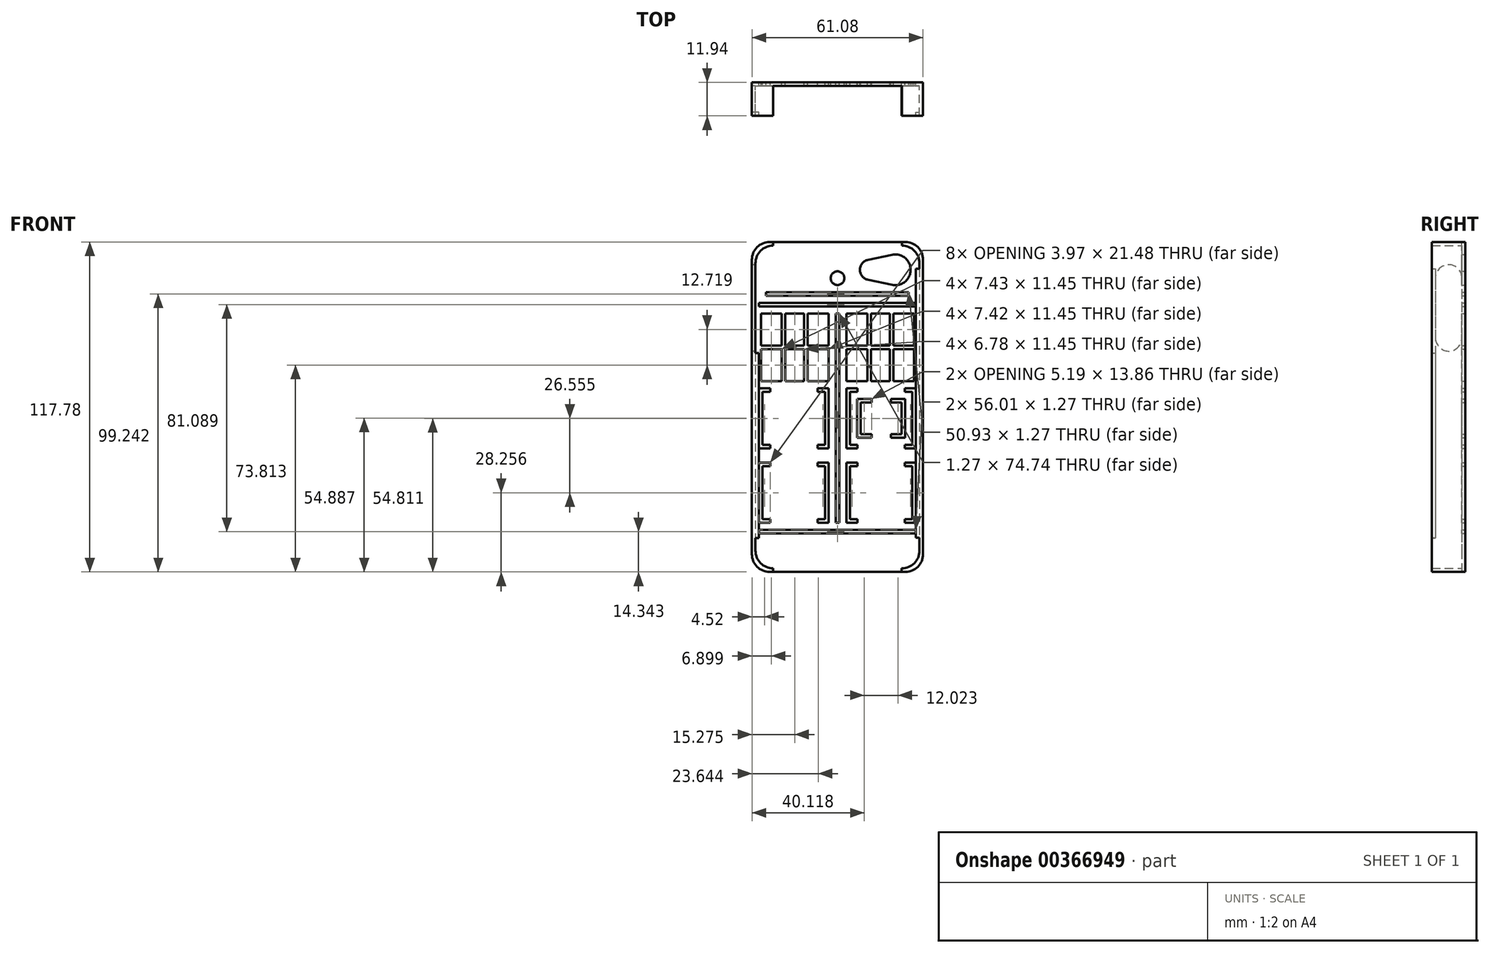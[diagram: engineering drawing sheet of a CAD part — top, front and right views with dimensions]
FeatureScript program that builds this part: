
annotation { "Feature Type Name" : "Feature", "Feature Type Description" : "" }
export const myFeature = defineFeature(function(context is Context, id is Id, definition is map)
    precondition{}
    {
        {
            var Q0;
            Q0=qCreatedBy(makeId("Front.planeOp"),FACE);
            var sketch = newSketch(context, id + "F0", { "sketchPlane" : qUnion([Q0])});
            skLineSegment(sketch, "E0.left", {"start": v(-75.12, 56.4) * mm, "end": v(-75.12, -46.14) * mm});
            skLineSegment(sketch, "E0.right", {"start": v(-16.58, 56.4) * mm, "end": v(-16.58, -46.14) * mm});
            skPoint(sketch, "E1.visualSharp", {"position": v(-16.58, 62.75) * mm});
            skArc(sketch, "E1.filletArc", {"start": v(-16.58, 56.4) * mm, "mid": v(-18.43, 60.88) * mm, "end": v(-22.9, 62.75) * mm});
            skPoint(sketch, "E2.visualSharp", {"position": v(-75.12, 62.75) * mm});
            skArc(sketch, "E2.filletArc", {"start": v(-68.77, 62.75) * mm, "mid": v(-73.26, 60.89) * mm, "end": v(-75.12, 56.4) * mm});
            skPoint(sketch, "E3.visualSharp", {"position": v(-75.12, -52.5) * mm});
            skArc(sketch, "E3.filletArc", {"start": v(-75.12, -46.14) * mm, "mid": v(-73.26, -50.63) * mm, "end": v(-68.77, -52.5) * mm});
            skPoint(sketch, "E4.visualSharp", {"position": v(-16.58, -52.5) * mm});
            skArc(sketch, "E4.filletArc", {"start": v(-22.93, -52.5) * mm, "mid": v(-18.44, -50.63) * mm, "end": v(-16.58, -46.14) * mm});
            skLineSegment(sketch, "E5.bottom", {"start": v(-70.04, 64.02) * mm, "end": v(-68.77, 64.02) * mm});
            skLineSegment(sketch, "E5.top", {"start": v(-70.04, -53.76) * mm, "end": v(-68.77, -53.76) * mm});
            skLineSegment(sketch, "E5.left", {"start": v(-76.4, 57.67) * mm, "end": v(-76.4, -47.41) * mm});
            skLineSegment(sketch, "E5.right", {"start": v(-15.3, 57.67) * mm, "end": v(-15.3, -47.41) * mm});
            skPoint(sketch, "E6.visualSharp", {"position": v(-15.3, 64.02) * mm});
            skArc(sketch, "E6.filletArc", {"start": v(-15.3, 57.67) * mm, "mid": v(-17.17, 62.16) * mm, "end": v(-21.66, 64.02) * mm});
            skPoint(sketch, "E7.visualSharp", {"position": v(-76.4, 64.02) * mm});
            skArc(sketch, "E7.filletArc", {"start": v(-70.04, 64.02) * mm, "mid": v(-74.53, 62.16) * mm, "end": v(-76.4, 57.67) * mm});
            skPoint(sketch, "E8.visualSharp", {"position": v(-76.4, -53.76) * mm});
            skArc(sketch, "E8.filletArc", {"start": v(-76.4, -47.41) * mm, "mid": v(-74.53, -51.9) * mm, "end": v(-70.04, -53.76) * mm});
            skPoint(sketch, "E9.visualSharp", {"position": v(-15.3, -53.76) * mm});
            skArc(sketch, "E9.filletArc", {"start": v(-21.66, -53.76) * mm, "mid": v(-17.17, -51.9) * mm, "end": v(-15.3, -47.41) * mm});
            skLineSegment(sketch, "E10", {"start": v(-68.77, -52.5) * mm, "end": v(-68.77, -53.76) * mm});
            skLineSegment(sketch, "E11", {"start": v(-22.93, -52.5) * mm, "end": v(-22.93, -53.76) * mm});
            skLineSegment(sketch, "E12.trimOffspring", {"start": v(-22.93, -53.76) * mm, "end": v(-21.66, -53.76) * mm});
            skLineSegment(sketch, "E13", {"start": v(-68.77, 62.75) * mm, "end": v(-68.77, 64.02) * mm});
            skLineSegment(sketch, "E14", {"start": v(-22.9, 62.75) * mm, "end": v(-22.9, 64.02) * mm});
            skLineSegment(sketch, "E15.trimOffspring", {"start": v(-22.9, 64.02) * mm, "end": v(-21.66, 64.02) * mm});
            skLineSegment(sketch, "E16", {"start": v(-68.77, 64.02) * mm, "end": v(-22.9, 64.02) * mm});
            skLineSegment(sketch, "E17", {"start": v(-68.77, -53.76) * mm, "end": v(-22.93, -53.76) * mm});
            skCircle(sketch, "E18", {"center": v(-25.24, 54.09) * mm, "radius": 5.48 * mm});
            skCircle(sketch, "E19", {"center": v(-34.23, 54.09) * mm, "radius": 3.64 * mm});
            skLineSegment(sketch, "E20", {"start": v(-26.36, 59.46) * mm, "end": v(-34.97, 57.65) * mm});
            skLineSegment(sketch, "E21", {"start": v(-26.36, 48.72) * mm, "end": v(-34.97, 50.53) * mm});
            skLineSegment(sketch, "E22", {"start": v(-22.9, 62.75) * mm, "end": v(-68.77, 62.75) * mm});
            skSolve(sketch);
        }
        {
            var Q0;
            Q0=makeQuery(id+"F0.imprint","IMPRINT",FACE,{"disambiguationData":[TD([[makeQuery(id+"F0.imprint","IMPRINT",EDGE,{"derivedFrom":sQuery(id+"F0.wireOp",EDGE,"E0.left")}),1.0]])]});
            extrude(context, id + "F1", {"entities" : qUnion([Q0]), "depth" : 1.27 * mm});
        }
        {
            var Q0;
            Q0=makeQuery(id+"F0.imprint","IMPRINT",FACE,{"disambiguationData":[TD([[makeQuery(id+"F0.imprint","IMPRINT",EDGE,{"derivedFrom":sQuery(id+"F0.wireOp",EDGE,"E0.left")}),-1.0]])]});
            var Q1;
            Q1=makeQuery(id+"F0.imprint","IMPRINT",FACE,{"disambiguationData":[TD([[makeQuery(id+"F0.imprint","IMPRINT",EDGE,{"derivedFrom":sQuery(id+"F0.wireOp",EDGE,"E0.right")}),1.0]])]});
            extrude(context, id + "F2", {"entities" : qUnion([Q0, Q1]), "operationType" : NewBodyOperationType.ADD, "depth" : 11.94 * mm});
        }
        {
            var Q0;
            Q0=makeQuery(id+"F2.opExtrude","SWEPT_FACE",FACE,{"disambiguationData":[OSD([sQuery(id+"F0.wireOp",EDGE,"E5.left")])]});
            var sketch = newSketch(context, id + "F3", { "sketchPlane" : qUnion([Q0])});
            skCircle(sketch, "E23", {"center": v(5.97, 51.22) * mm, "radius": 4.7 * mm});
            skCircle(sketch, "E24", {"center": v(5.97, 29.75) * mm, "radius": 4.7 * mm});
            skLineSegment(sketch, "E25", {"start": v(1.27, 51.22) * mm, "end": v(1.27, 29.75) * mm});
            skLineSegment(sketch, "E26", {"start": v(10.67, 29.75) * mm, "end": v(10.67, 51.22) * mm});
            skSolve(sketch);
        }
        {
            var Q0;
            {var subQ0=sQuery(id+"F3.wireOp",EDGE,"E25");Q0=makeQuery(id+"F3.imprint","IMPRINT",FACE,{"disambiguationData":[TD([[makeQuery(id+"F3.imprint","IMPRINT",EDGE,{"derivedFrom":subQ0}),1.0]])]});}
            var Q1;
            {var subQ0=sQuery(id+"F3.wireOp",EDGE,"E23");var subQ1=makeQuery(id+"F3.imprint","INTERSECT",VERTEX,{"derivedFrom":[subQ0,sQuery(id+"F3.wireOp",EDGE,"E25")]});Q1=makeQuery(id+"F3.imprint","IMPRINT",FACE,{"disambiguationData":[TD([[makeQuery(id+"F3.imprint","IMPRINT",EDGE,{"disambiguationData":[TD([[subQ1,1.0]])],"derivedFrom":subQ0}),1.0]])]});}
            var Q2;
            {var subQ0=sQuery(id+"F3.wireOp",EDGE,"E24");var subQ1=makeQuery(id+"F3.imprint","INTERSECT",VERTEX,{"derivedFrom":[subQ0,sQuery(id+"F3.wireOp",EDGE,"E25")]});Q2=makeQuery(id+"F3.imprint","IMPRINT",FACE,{"disambiguationData":[TD([[makeQuery(id+"F3.imprint","IMPRINT",EDGE,{"disambiguationData":[TD([[subQ1,1.0]])],"derivedFrom":subQ0}),1.0]])]});}
            extrude(context, id + "F4", {"entities" : qUnion([Q0, Q1, Q2]), "operationType" : NewBodyOperationType.REMOVE, "oppositeDirection" : true, "depth" : 25.4 * mm});
        }
        {
            var Q0;
            Q0=makeQuery(id+"F0.imprint","IMPRINT",FACE,{"disambiguationData":[TD([[makeQuery(id+"F0.imprint","IMPRINT",EDGE,{"derivedFrom":sQuery(id+"F0.wireOp",EDGE,"E0.right")}),-1.0]])]});
            var Q1;
            Q1=makeQuery(id+"F0.imprint","IMPRINT",FACE,{"disambiguationData":[TD([[makeQuery(id+"F0.imprint","IMPRINT",EDGE,{"derivedFrom":sQuery(id+"F0.wireOp",EDGE,"E13")}),-1.0]])]});
            extrude(context, id + "F5", {"entities" : qUnion([Q0, Q1]), "depth" : 1.27 * mm});
        }
        {
            var Q0;
            Q0=makeQuery(id+"F2.opExtrude","SWEPT_FACE",FACE,{"disambiguationData":[OSD([sQuery(id+"F0.wireOp",EDGE,"E0.left")])]});
            var sketch = newSketch(context, id + "F6", { "sketchPlane" : qUnion([Q0])});
            skLineSegment(sketch, "E27.bottom", {"start": v(-11.94, 24.38) * mm, "end": v(-10.67, 24.38) * mm});
            skLineSegment(sketch, "E27.top", {"start": v(-11.94, -41.62) * mm, "end": v(-10.67, -41.62) * mm});
            skLineSegment(sketch, "E27.left", {"start": v(-11.94, 24.38) * mm, "end": v(-11.94, -41.62) * mm});
            skLineSegment(sketch, "E27.right", {"start": v(-10.67, 24.38) * mm, "end": v(-10.67, -41.62) * mm});
            skSolve(sketch);
        }
        {
            var Q0;
            Q0=makeQuery(id+"F6.imprint","IMPRINT",FACE,{"disambiguationData":[TD([[makeQuery(id+"F6.imprint","IMPRINT",EDGE,{"derivedFrom":sQuery(id+"F6.wireOp",EDGE,"E27.bottom")}),-1.0]])]});
            extrude(context, id + "F7", {"entities" : qUnion([Q0]), "operationType" : NewBodyOperationType.ADD, "depth" : 1.27 * mm});
        }
        {
            var Q0;
            Q0=makeQuery(id+"F2.opExtrude","SWEPT_FACE",FACE,{"disambiguationData":[OSD([sQuery(id+"F0.wireOp",EDGE,"E0.right")])]});
            var sketch = newSketch(context, id + "F8", { "sketchPlane" : qUnion([Q0])});
            skLineSegment(sketch, "E28.bottom", {"start": v(11.94, 54.52) * mm, "end": v(10.67, 54.52) * mm});
            skLineSegment(sketch, "E28.top", {"start": v(11.94, -41.5) * mm, "end": v(10.67, -41.5) * mm});
            skLineSegment(sketch, "E28.left", {"start": v(11.94, 54.52) * mm, "end": v(11.94, -41.5) * mm});
            skLineSegment(sketch, "E28.right", {"start": v(10.67, 54.52) * mm, "end": v(10.67, -41.5) * mm});
            skSolve(sketch);
        }
        {
            var Q0;
            Q0=makeQuery(id+"F8.imprint","IMPRINT",FACE,{"disambiguationData":[TD([[makeQuery(id+"F8.imprint","IMPRINT",EDGE,{"derivedFrom":sQuery(id+"F8.wireOp",EDGE,"E28.bottom")}),1.0]])]});
            extrude(context, id + "F9", {"entities" : qUnion([Q0]), "operationType" : NewBodyOperationType.ADD, "depth" : 1.27 * mm});
        }
        {
            var Q0;
            {var subQ0=sQuery(id+"F0.wireOp",EDGE,"E14");var subQ1=sQuery(id+"F0.wireOp",EDGE,"E11");var subQ2=sQuery(id+"F0.wireOp",EDGE,"E4.filletArc");var subQ3=sQuery(id+"F0.wireOp",EDGE,"E1.filletArc");var subQ4=sQuery(id+"F0.wireOp",EDGE,"E0.right");var subQ5=sQuery(id+"F0.wireOp",EDGE,"E13");var subQ6=sQuery(id+"F0.wireOp",EDGE,"E10");var subQ7=sQuery(id+"F0.wireOp",EDGE,"E3.filletArc");var subQ8=sQuery(id+"F0.wireOp",EDGE,"E2.filletArc");var subQ9=sQuery(id+"F0.wireOp",EDGE,"E0.left");Q0=makeQuery(id+"F2.boolean.opBoolean","MERGE",FACE,{"derivedFrom":[makeQuery(id+"F1.opExtrude","CAP_FACE",FACE,{"disambiguationData":[OSD([subQ9,subQ4,subQ3,subQ8,subQ7,subQ2,subQ6,subQ1,subQ5,subQ0,sQuery(id+"F0.wireOp",EDGE,"E16"),sQuery(id+"F0.wireOp",EDGE,"E17"),sQuery(id+"F0.wireOp",EDGE,"E18"),sQuery(id+"F0.wireOp",EDGE,"E19"),sQuery(id+"F0.wireOp",EDGE,"E20"),sQuery(id+"F0.wireOp",EDGE,"E21")])],"isStart":true}),makeQuery(id+"F2.opExtrude","CAP_FACE",FACE,{"disambiguationData":[OSD([subQ9,subQ8,subQ7,sQuery(id+"F0.wireOp",EDGE,"E5.bottom"),sQuery(id+"F0.wireOp",EDGE,"E5.top"),sQuery(id+"F0.wireOp",EDGE,"E5.left"),sQuery(id+"F0.wireOp",EDGE,"E7.filletArc"),sQuery(id+"F0.wireOp",EDGE,"E8.filletArc"),subQ6,subQ5])],"isStart":true}),makeQuery(id+"F2.opExtrude","CAP_FACE",FACE,{"disambiguationData":[OSD([subQ4,subQ3,subQ2,sQuery(id+"F0.wireOp",EDGE,"E5.right"),sQuery(id+"F0.wireOp",EDGE,"E6.filletArc"),sQuery(id+"F0.wireOp",EDGE,"E9.filletArc"),subQ1,sQuery(id+"F0.wireOp",EDGE,"E12.trimOffspring"),subQ0,sQuery(id+"F0.wireOp",EDGE,"E15.trimOffspring")])],"isStart":true})]});}
            var sketch = newSketch(context, id + "F10", { "sketchPlane" : qUnion([Q0])});
            skLineSegment(sketch, "E29", {"start": v(45.85, 64.02) * mm, "end": v(45.85, -53.76) * mm});
            skLineSegment(sketch, "E30.bottom", {"start": v(18.5, 38.5) * mm, "end": v(42.66, 38.5) * mm});
            skLineSegment(sketch, "E30.top", {"start": v(18.5, 14.33) * mm, "end": v(42.66, 14.33) * mm});
            skLineSegment(sketch, "E30.left", {"start": v(18.5, 38.5) * mm, "end": v(18.5, 14.33) * mm});
            skLineSegment(sketch, "E30.right", {"start": v(42.66, 38.5) * mm, "end": v(42.66, 14.33) * mm});
            skLineSegment(sketch, "E31.bottom", {"start": v(49.04, 38.5) * mm, "end": v(73.2, 38.5) * mm});
            skLineSegment(sketch, "E31.top", {"start": v(49.04, 14.33) * mm, "end": v(73.2, 14.33) * mm});
            skLineSegment(sketch, "E31.left", {"start": v(49.04, 38.5) * mm, "end": v(49.04, 14.33) * mm});
            skLineSegment(sketch, "E31.right", {"start": v(73.2, 38.5) * mm, "end": v(73.2, 14.33) * mm});
            skLineSegment(sketch, "E32", {"start": v(18.5, 38.5) * mm, "end": v(15.3, 38.5) * mm});
            skLineSegment(sketch, "E33", {"start": v(42.66, 38.5) * mm, "end": v(45.85, 38.5) * mm});
            skLineSegment(sketch, "E34", {"start": v(45.85, 38.5) * mm, "end": v(49.04, 38.5) * mm});
            skLineSegment(sketch, "E35", {"start": v(73.2, 38.5) * mm, "end": v(76.4, 38.5) * mm});
            skLineSegment(sketch, "E36", {"start": v(18.5, 26.41) * mm, "end": v(42.66, 26.41) * mm});
            skLineSegment(sketch, "E37", {"start": v(26.55, 38.5) * mm, "end": v(26.55, 14.33) * mm});
            skLineSegment(sketch, "E38", {"start": v(34.6, 38.5) * mm, "end": v(34.6, 14.33) * mm});
            skLineSegment(sketch, "E39", {"start": v(25.91, 38.5) * mm, "end": v(25.91, 26.41) * mm});
            skLineSegment(sketch, "E40", {"start": v(27.18, 38.5) * mm, "end": v(27.18, 26.41) * mm});
            skLineSegment(sketch, "E41", {"start": v(33.96, 38.5) * mm, "end": v(33.96, 26.41) * mm});
            skLineSegment(sketch, "E42", {"start": v(35.23, 38.5) * mm, "end": v(35.23, 26.41) * mm});
            skLineSegment(sketch, "E43", {"start": v(18.5, 27.05) * mm, "end": v(42.66, 27.05) * mm});
            skLineSegment(sketch, "E44", {"start": v(25.91, 26.41) * mm, "end": v(25.91, 14.33) * mm});
            skLineSegment(sketch, "E45", {"start": v(27.18, 26.41) * mm, "end": v(27.18, 14.33) * mm});
            skLineSegment(sketch, "E46", {"start": v(33.96, 26.41) * mm, "end": v(33.96, 14.33) * mm});
            skLineSegment(sketch, "E47", {"start": v(35.23, 26.41) * mm, "end": v(35.23, 14.33) * mm});
            skLineSegment(sketch, "E48", {"start": v(18.5, 25.78) * mm, "end": v(42.66, 25.78) * mm});
            skLineSegment(sketch, "E49", {"start": v(49.04, 26.41) * mm, "end": v(73.2, 26.41) * mm});
            skLineSegment(sketch, "E50", {"start": v(57.09, 38.5) * mm, "end": v(57.09, 14.33) * mm});
            skLineSegment(sketch, "E51", {"start": v(65.14, 38.5) * mm, "end": v(65.14, 14.33) * mm});
            skLineSegment(sketch, "E52", {"start": v(56.45, 38.5) * mm, "end": v(56.45, 14.33) * mm});
            skLineSegment(sketch, "E53", {"start": v(57.72, 38.5) * mm, "end": v(57.72, 14.33) * mm});
            skLineSegment(sketch, "E54", {"start": v(64.5, 38.5) * mm, "end": v(64.5, 14.33) * mm});
            skLineSegment(sketch, "E55", {"start": v(65.78, 38.5) * mm, "end": v(65.78, 14.33) * mm});
            skLineSegment(sketch, "E56", {"start": v(49.04, 27.05) * mm, "end": v(73.2, 27.05) * mm});
            skLineSegment(sketch, "E57", {"start": v(49.04, 25.78) * mm, "end": v(73.2, 25.78) * mm});
            skLineSegment(sketch, "E58", {"start": v(17.85, -40.05) * mm, "end": v(73.85, -40.05) * mm});
            skLineSegment(sketch, "E59", {"start": v(73.85, -40.05) * mm, "end": v(73.85, -38.78) * mm});
            skLineSegment(sketch, "E60", {"start": v(73.85, -38.78) * mm, "end": v(17.85, -38.78) * mm});
            skLineSegment(sketch, "E61", {"start": v(17.85, -38.78) * mm, "end": v(17.85, -40.05) * mm});
            skLineSegment(sketch, "E62", {"start": v(45.21, 38.5) * mm, "end": v(45.21, -38.78) * mm});
            skLineSegment(sketch, "E63.MirrorCS", {"start": v(46.48, 38.5) * mm, "end": v(46.48, -38.78) * mm});
            skLineSegment(sketch, "E64", {"start": v(17.85, 41.04) * mm, "end": v(73.85, 41.04) * mm});
            skLineSegment(sketch, "E65", {"start": v(73.85, 41.04) * mm, "end": v(73.85, 42.3) * mm});
            skLineSegment(sketch, "E66", {"start": v(73.85, 42.3) * mm, "end": v(17.85, 42.3) * mm});
            skLineSegment(sketch, "E67", {"start": v(17.85, 42.3) * mm, "end": v(17.85, 41.04) * mm});
            skLineSegment(sketch, "E68", {"start": v(20.39, 44.85) * mm, "end": v(71.31, 44.85) * mm});
            skLineSegment(sketch, "E69", {"start": v(71.31, 44.85) * mm, "end": v(71.31, 46.12) * mm});
            skLineSegment(sketch, "E70", {"start": v(71.31, 46.12) * mm, "end": v(20.39, 46.12) * mm});
            skLineSegment(sketch, "E71", {"start": v(20.39, 46.12) * mm, "end": v(20.39, 44.85) * mm});
            skLineSegment(sketch, "E72", {"start": v(45.21, -36.24) * mm, "end": v(46.48, -36.24) * mm});
            skLineSegment(sketch, "E73", {"start": v(18.5, 14.33) * mm, "end": v(15.3, 14.33) * mm});
            skLineSegment(sketch, "E74", {"start": v(17.85, -38.78) * mm, "end": v(15.3, -38.78) * mm});
            skLineSegment(sketch, "E75", {"start": v(73.2, 14.33) * mm, "end": v(76.4, 14.33) * mm});
            skLineSegment(sketch, "E76", {"start": v(73.85, -38.78) * mm, "end": v(76.4, -38.78) * mm});
            skLineSegment(sketch, "E77", {"start": v(15.3, 14.33) * mm, "end": v(15.3, -38.78) * mm});
            skLineSegment(sketch, "E78", {"start": v(15.3, -12.23) * mm, "end": v(76.4, -12.23) * mm});
            skLineSegment(sketch, "E79", {"start": v(45.21, -12.23) * mm, "end": v(15.3, -12.23) * mm});
            skLineSegment(sketch, "E80", {"start": v(30.26, -12.23) * mm, "end": v(30.26, -38.78) * mm});
            skLineSegment(sketch, "E81", {"start": v(21.81, -14.77) * mm, "end": v(17.85, -14.77) * mm});
            skLineSegment(sketch, "E82", {"start": v(17.85, -14.77) * mm, "end": v(17.85, -36.24) * mm});
            skLineSegment(sketch, "E83", {"start": v(17.85, -36.24) * mm, "end": v(21.81, -36.24) * mm});
            skLineSegment(sketch, "E84", {"start": v(21.81, -36.24) * mm, "end": v(21.81, -34.97) * mm});
            skLineSegment(sketch, "E85", {"start": v(21.81, -34.97) * mm, "end": v(19.12, -34.97) * mm});
            skLineSegment(sketch, "E86", {"start": v(19.12, -34.97) * mm, "end": v(19.12, -16.04) * mm});
            skLineSegment(sketch, "E87", {"start": v(19.12, -16.04) * mm, "end": v(21.81, -16.04) * mm});
            skLineSegment(sketch, "E88", {"start": v(21.81, -16.04) * mm, "end": v(21.81, -14.77) * mm});
            skLineSegment(sketch, "E89.MirrorCS", {"start": v(38.7, -14.77) * mm, "end": v(42.67, -14.77) * mm});
            skLineSegment(sketch, "E90.MirrorCS", {"start": v(38.7, -16.04) * mm, "end": v(38.7, -14.77) * mm});
            skLineSegment(sketch, "E91.MirrorCS", {"start": v(41.4, -16.04) * mm, "end": v(38.7, -16.04) * mm});
            skLineSegment(sketch, "E92.MirrorCS", {"start": v(41.4, -34.97) * mm, "end": v(41.4, -16.04) * mm});
            skLineSegment(sketch, "E93.MirrorCS", {"start": v(42.67, -14.77) * mm, "end": v(42.67, -36.24) * mm});
            skLineSegment(sketch, "E94.MirrorCS", {"start": v(38.7, -34.97) * mm, "end": v(41.4, -34.97) * mm});
            skLineSegment(sketch, "E95.MirrorCS", {"start": v(38.7, -36.24) * mm, "end": v(38.7, -34.97) * mm});
            skLineSegment(sketch, "E96.MirrorCS", {"start": v(42.67, -36.24) * mm, "end": v(38.7, -36.24) * mm});
            skLineSegment(sketch, "E97.MirrorCS", {"start": v(53, -16.04) * mm, "end": v(53, -14.77) * mm});
            skLineSegment(sketch, "E98.MirrorCS", {"start": v(53, -14.77) * mm, "end": v(49.02, -14.77) * mm});
            skLineSegment(sketch, "E99.MirrorCS", {"start": v(50.3, -16.04) * mm, "end": v(53, -16.04) * mm});
            skLineSegment(sketch, "E100.MirrorCS", {"start": v(53, -36.24) * mm, "end": v(53, -34.97) * mm});
            skLineSegment(sketch, "E101.MirrorCS", {"start": v(53, -34.97) * mm, "end": v(50.3, -34.97) * mm});
            skLineSegment(sketch, "E102.MirrorCS", {"start": v(49.02, -36.24) * mm, "end": v(53, -36.24) * mm});
            skLineSegment(sketch, "E103.MirrorCS", {"start": v(49.02, -14.77) * mm, "end": v(49.02, -36.24) * mm});
            skLineSegment(sketch, "E104.MirrorCS", {"start": v(50.3, -34.97) * mm, "end": v(50.3, -16.04) * mm});
            skLineSegment(sketch, "E105.MirrorCS", {"start": v(69.89, -36.24) * mm, "end": v(69.89, -34.97) * mm});
            skLineSegment(sketch, "E106.MirrorCS", {"start": v(69.89, -16.04) * mm, "end": v(69.89, -14.77) * mm});
            skLineSegment(sketch, "E107.MirrorCS", {"start": v(73.85, -36.24) * mm, "end": v(69.89, -36.24) * mm});
            skLineSegment(sketch, "E108.MirrorCS", {"start": v(72.58, -16.04) * mm, "end": v(69.89, -16.04) * mm});
            skLineSegment(sketch, "E109.MirrorCS", {"start": v(72.58, -34.97) * mm, "end": v(72.58, -16.04) * mm});
            skLineSegment(sketch, "E110.MirrorCS", {"start": v(69.89, -34.97) * mm, "end": v(72.58, -34.97) * mm});
            skLineSegment(sketch, "E111.MirrorCS", {"start": v(69.89, -14.77) * mm, "end": v(73.85, -14.77) * mm});
            skLineSegment(sketch, "E112.MirrorCS", {"start": v(73.85, -14.77) * mm, "end": v(73.85, -36.24) * mm});
            skLineSegment(sketch, "E113.MirrorCS", {"start": v(53, -8.42) * mm, "end": v(53, -9.69) * mm});
            skLineSegment(sketch, "E114.MirrorCS", {"start": v(50.3, -8.42) * mm, "end": v(53, -8.42) * mm});
            skLineSegment(sketch, "E115.MirrorCS", {"start": v(53, -9.69) * mm, "end": v(49.02, -9.69) * mm});
            skLineSegment(sketch, "E116.MirrorCS", {"start": v(53, 11.79) * mm, "end": v(53, 10.52) * mm});
            skLineSegment(sketch, "E117.MirrorCS", {"start": v(50.3, 10.52) * mm, "end": v(50.3, -8.42) * mm});
            skLineSegment(sketch, "E118.MirrorCS", {"start": v(49.02, 11.79) * mm, "end": v(53, 11.79) * mm});
            skLineSegment(sketch, "E119.MirrorCS", {"start": v(53, 10.52) * mm, "end": v(50.3, 10.52) * mm});
            skLineSegment(sketch, "E120.MirrorCS", {"start": v(49.02, -9.69) * mm, "end": v(49.02, 11.79) * mm});
            skLineSegment(sketch, "E121.MirrorCS", {"start": v(69.89, 11.79) * mm, "end": v(69.89, 10.52) * mm});
            skLineSegment(sketch, "E122.MirrorCS", {"start": v(69.89, 10.52) * mm, "end": v(72.58, 10.52) * mm});
            skLineSegment(sketch, "E123.MirrorCS", {"start": v(73.85, 11.79) * mm, "end": v(69.89, 11.79) * mm});
            skLineSegment(sketch, "E124.MirrorCS", {"start": v(73.85, -9.69) * mm, "end": v(73.85, 11.79) * mm});
            skLineSegment(sketch, "E125.MirrorCS", {"start": v(72.58, 10.52) * mm, "end": v(72.58, -8.42) * mm});
            skLineSegment(sketch, "E126.MirrorCS", {"start": v(69.89, -9.69) * mm, "end": v(73.85, -9.69) * mm});
            skLineSegment(sketch, "E127.MirrorCS", {"start": v(72.58, -8.42) * mm, "end": v(69.89, -8.42) * mm});
            skLineSegment(sketch, "E128.MirrorCS", {"start": v(69.89, -8.42) * mm, "end": v(69.89, -9.69) * mm});
            skLineSegment(sketch, "E129.MirrorCS", {"start": v(38.7, -8.42) * mm, "end": v(38.7, -9.69) * mm});
            skLineSegment(sketch, "E130.MirrorCS", {"start": v(38.7, -9.69) * mm, "end": v(42.67, -9.69) * mm});
            skLineSegment(sketch, "E131.MirrorCS", {"start": v(41.4, -8.42) * mm, "end": v(38.7, -8.42) * mm});
            skLineSegment(sketch, "E132.MirrorCS", {"start": v(38.7, 11.79) * mm, "end": v(38.7, 10.52) * mm});
            skLineSegment(sketch, "E133.MirrorCS", {"start": v(41.4, 10.52) * mm, "end": v(41.4, -8.42) * mm});
            skLineSegment(sketch, "E134.MirrorCS", {"start": v(38.7, 10.52) * mm, "end": v(41.4, 10.52) * mm});
            skLineSegment(sketch, "E135.MirrorCS", {"start": v(42.67, -9.69) * mm, "end": v(42.67, 11.79) * mm});
            skLineSegment(sketch, "E136.MirrorCS", {"start": v(42.67, 11.79) * mm, "end": v(38.7, 11.79) * mm});
            skLineSegment(sketch, "E137.MirrorCS", {"start": v(21.81, 11.79) * mm, "end": v(21.81, 10.52) * mm});
            skLineSegment(sketch, "E138.MirrorCS", {"start": v(21.81, -8.42) * mm, "end": v(21.81, -9.69) * mm});
            skLineSegment(sketch, "E139.MirrorCS", {"start": v(17.85, -9.69) * mm, "end": v(17.85, 11.79) * mm});
            skLineSegment(sketch, "E140.MirrorCS", {"start": v(19.12, 10.52) * mm, "end": v(19.12, -8.42) * mm});
            skLineSegment(sketch, "E141.MirrorCS", {"start": v(21.81, 10.52) * mm, "end": v(19.12, 10.52) * mm});
            skLineSegment(sketch, "E142.MirrorCS", {"start": v(19.12, -8.42) * mm, "end": v(21.81, -8.42) * mm});
            skLineSegment(sketch, "E143.MirrorCS", {"start": v(17.85, 11.79) * mm, "end": v(21.81, 11.79) * mm});
            skLineSegment(sketch, "E144.MirrorCS", {"start": v(21.81, -9.69) * mm, "end": v(17.85, -9.69) * mm});
            skLineSegment(sketch, "E145", {"start": v(21.66, 7.98) * mm, "end": v(21.66, -5.88) * mm});
            skLineSegment(sketch, "E146", {"start": v(21.66, -5.88) * mm, "end": v(26.84, -5.88) * mm});
            skLineSegment(sketch, "E147", {"start": v(26.84, -5.88) * mm, "end": v(26.84, -4.6) * mm});
            skLineSegment(sketch, "E148", {"start": v(26.84, -4.6) * mm, "end": v(22.93, -4.6) * mm});
            skLineSegment(sketch, "E149", {"start": v(22.93, -4.6) * mm, "end": v(22.93, 6.7) * mm});
            skLineSegment(sketch, "E150", {"start": v(22.93, 6.7) * mm, "end": v(26.84, 6.7) * mm});
            skLineSegment(sketch, "E151", {"start": v(26.84, 6.7) * mm, "end": v(26.84, 7.98) * mm});
            skLineSegment(sketch, "E152", {"start": v(26.84, 7.98) * mm, "end": v(21.66, 7.98) * mm});
            skLineSegment(sketch, "E153", {"start": v(30.26, -12.23) * mm, "end": v(30.26, 14.33) * mm});
            skLineSegment(sketch, "E154.MirrorCS", {"start": v(33.68, 6.7) * mm, "end": v(33.68, 7.98) * mm});
            skLineSegment(sketch, "E155.MirrorCS", {"start": v(33.68, -5.88) * mm, "end": v(33.68, -4.6) * mm});
            skLineSegment(sketch, "E156.MirrorCS", {"start": v(38.86, -5.88) * mm, "end": v(33.68, -5.88) * mm});
            skLineSegment(sketch, "E157.MirrorCS", {"start": v(38.86, 7.98) * mm, "end": v(38.86, -5.88) * mm});
            skLineSegment(sketch, "E158.MirrorCS", {"start": v(37.6, 6.7) * mm, "end": v(33.68, 6.7) * mm});
            skLineSegment(sketch, "E159.MirrorCS", {"start": v(33.68, 7.98) * mm, "end": v(38.86, 7.98) * mm});
            skLineSegment(sketch, "E160.MirrorCS", {"start": v(37.6, -4.6) * mm, "end": v(37.6, 6.7) * mm});
            skLineSegment(sketch, "E161.MirrorCS", {"start": v(33.68, -4.6) * mm, "end": v(37.6, -4.6) * mm});
            skCircle(sketch, "E162", {"center": v(45.85, 51.1) * mm, "radius": 2.44 * mm});
            skSolve(sketch);
        }
        {
            var Q0;
            {var subQ1=sQuery(id+"F10.wireOp",EDGE,"E30.bottom");var subQ3=sQuery(id+"F10.wireOp",EDGE,"E39");var subQ4=makeQuery(id+"F10.imprint","INTERSECT",VERTEX,{"derivedFrom":[subQ1,subQ3]});Q0=makeQuery(id+"F10.imprint","IMPRINT",FACE,{"disambiguationData":[TD([[makeQuery(id+"F10.imprint","IMPRINT",EDGE,{"disambiguationData":[TD([[subQ4,-1.0]])],"derivedFrom":subQ3}),-1.0]])]});}
            var Q1;
            {var subQ0=sQuery(id+"F10.wireOp",EDGE,"E40");var subQ1=sQuery(id+"F10.wireOp",EDGE,"E30.bottom");var subQ2=makeQuery(id+"F10.imprint","INTERSECT",VERTEX,{"derivedFrom":[subQ1,subQ0]});Q1=makeQuery(id+"F10.imprint","IMPRINT",FACE,{"disambiguationData":[TD([[makeQuery(id+"F10.imprint","IMPRINT",EDGE,{"disambiguationData":[TD([[subQ2,-1.0]])],"derivedFrom":subQ1}),-1.0]])]});}
            var Q2;
            {var subQ1=sQuery(id+"F10.wireOp",EDGE,"E30.bottom");var subQ3=sQuery(id+"F10.wireOp",EDGE,"E42");var subQ4=makeQuery(id+"F10.imprint","INTERSECT",VERTEX,{"derivedFrom":[subQ1,subQ3]});Q2=makeQuery(id+"F10.imprint","IMPRINT",FACE,{"disambiguationData":[TD([[makeQuery(id+"F10.imprint","IMPRINT",EDGE,{"disambiguationData":[TD([[subQ4,-1.0]])],"derivedFrom":subQ3}),1.0]])]});}
            var Q3;
            {var subQ0=sQuery(id+"F10.wireOp",EDGE,"E30.right");var subQ1=sQuery(id+"F10.wireOp",EDGE,"E30.top");var subQ2=makeQuery(id+"F10.imprint","INTERSECT",VERTEX,{"derivedFrom":[subQ1,subQ0]});Q3=makeQuery(id+"F10.imprint","IMPRINT",FACE,{"disambiguationData":[TD([[makeQuery(id+"F10.imprint","IMPRINT",EDGE,{"disambiguationData":[TD([[subQ2,1.0]])],"derivedFrom":subQ1}),1.0]])]});}
            var Q4;
            {var subQ0=sQuery(id+"F10.wireOp",EDGE,"E45");var subQ1=sQuery(id+"F10.wireOp",EDGE,"E30.top");var subQ2=makeQuery(id+"F10.imprint","INTERSECT",VERTEX,{"derivedFrom":[subQ1,subQ0]});Q4=makeQuery(id+"F10.imprint","IMPRINT",FACE,{"disambiguationData":[TD([[makeQuery(id+"F10.imprint","IMPRINT",EDGE,{"disambiguationData":[TD([[subQ2,-1.0]])],"derivedFrom":subQ1}),1.0]])]});}
            var Q5;
            {var subQ0=sQuery(id+"F10.wireOp",EDGE,"E30.left");var subQ1=sQuery(id+"F10.wireOp",EDGE,"E30.top");var subQ2=makeQuery(id+"F10.imprint","INTERSECT",VERTEX,{"derivedFrom":[subQ1,subQ0]});Q5=makeQuery(id+"F10.imprint","IMPRINT",FACE,{"disambiguationData":[TD([[makeQuery(id+"F10.imprint","IMPRINT",EDGE,{"disambiguationData":[TD([[subQ2,-1.0]])],"derivedFrom":subQ1}),1.0]])]});}
            var Q6;
            {var subQ1=sQuery(id+"F10.wireOp",EDGE,"E31.bottom");var subQ3=sQuery(id+"F10.wireOp",EDGE,"E52");var subQ4=makeQuery(id+"F10.imprint","INTERSECT",VERTEX,{"derivedFrom":[subQ1,subQ3]});Q6=makeQuery(id+"F10.imprint","IMPRINT",FACE,{"disambiguationData":[TD([[makeQuery(id+"F10.imprint","IMPRINT",EDGE,{"disambiguationData":[TD([[subQ4,-1.0]])],"derivedFrom":subQ3}),-1.0]])]});}
            var Q7;
            {var subQ0=sQuery(id+"F10.wireOp",EDGE,"E53");var subQ1=sQuery(id+"F10.wireOp",EDGE,"E31.bottom");var subQ2=makeQuery(id+"F10.imprint","INTERSECT",VERTEX,{"derivedFrom":[subQ1,subQ0]});Q7=makeQuery(id+"F10.imprint","IMPRINT",FACE,{"disambiguationData":[TD([[makeQuery(id+"F10.imprint","IMPRINT",EDGE,{"disambiguationData":[TD([[subQ2,-1.0]])],"derivedFrom":subQ1}),-1.0]])]});}
            var Q8;
            {var subQ1=sQuery(id+"F10.wireOp",EDGE,"E31.bottom");var subQ3=sQuery(id+"F10.wireOp",EDGE,"E55");var subQ4=makeQuery(id+"F10.imprint","INTERSECT",VERTEX,{"derivedFrom":[subQ1,subQ3]});Q8=makeQuery(id+"F10.imprint","IMPRINT",FACE,{"disambiguationData":[TD([[makeQuery(id+"F10.imprint","IMPRINT",EDGE,{"disambiguationData":[TD([[subQ4,-1.0]])],"derivedFrom":subQ3}),1.0]])]});}
            var Q9;
            {var subQ0=sQuery(id+"F10.wireOp",EDGE,"E31.right");var subQ1=sQuery(id+"F10.wireOp",EDGE,"E31.top");var subQ2=makeQuery(id+"F10.imprint","INTERSECT",VERTEX,{"derivedFrom":[subQ1,subQ0]});Q9=makeQuery(id+"F10.imprint","IMPRINT",FACE,{"disambiguationData":[TD([[makeQuery(id+"F10.imprint","IMPRINT",EDGE,{"disambiguationData":[TD([[subQ2,1.0]])],"derivedFrom":subQ1}),1.0]])]});}
            var Q10;
            {var subQ0=sQuery(id+"F10.wireOp",EDGE,"E53");var subQ1=sQuery(id+"F10.wireOp",EDGE,"E31.top");var subQ2=makeQuery(id+"F10.imprint","INTERSECT",VERTEX,{"derivedFrom":[subQ1,subQ0]});Q10=makeQuery(id+"F10.imprint","IMPRINT",FACE,{"disambiguationData":[TD([[makeQuery(id+"F10.imprint","IMPRINT",EDGE,{"disambiguationData":[TD([[subQ2,-1.0]])],"derivedFrom":subQ1}),1.0]])]});}
            var Q11;
            {var subQ0=sQuery(id+"F10.wireOp",EDGE,"E31.left");var subQ1=sQuery(id+"F10.wireOp",EDGE,"E31.top");var subQ2=makeQuery(id+"F10.imprint","INTERSECT",VERTEX,{"derivedFrom":[subQ1,subQ0]});Q11=makeQuery(id+"F10.imprint","IMPRINT",FACE,{"disambiguationData":[TD([[makeQuery(id+"F10.imprint","IMPRINT",EDGE,{"disambiguationData":[TD([[subQ2,-1.0]])],"derivedFrom":subQ1}),1.0]])]});}
            extrude(context, id + "F11", {"entities" : qUnion([Q0, Q1, Q2, Q3, Q4, Q5, Q6, Q7, Q8, Q9, Q10, Q11]), "operationType" : NewBodyOperationType.REMOVE, "oppositeDirection" : true, "depth" : 25.4 * mm});
        }
        {
            var Q0;
            {var subQ0=sQuery(id+"F10.wireOp",EDGE,"E34");var subQ5=sQuery(id+"F10.wireOp",EDGE,"E63.MirrorCS");var subQ6=makeQuery(id+"F10.imprint","INTERSECT",VERTEX,{"derivedFrom":[subQ0,subQ5]});Q0=makeQuery(id+"F10.imprint","IMPRINT",FACE,{"disambiguationData":[TD([[makeQuery(id+"F10.imprint","IMPRINT",EDGE,{"disambiguationData":[TD([[subQ6,-1.0]])],"derivedFrom":subQ5}),-1.0]])]});}
            var Q1;
            {var subQ5=sQuery(id+"F10.wireOp",EDGE,"E71");Q1=makeQuery(id+"F10.imprint","IMPRINT",FACE,{"disambiguationData":[TD([[makeQuery(id+"F10.imprint","IMPRINT",EDGE,{"derivedFrom":subQ5}),1.0]])]});}
            var Q2;
            {var subQ5=sQuery(id+"F10.wireOp",EDGE,"E69");Q2=makeQuery(id+"F10.imprint","IMPRINT",FACE,{"disambiguationData":[TD([[makeQuery(id+"F10.imprint","IMPRINT",EDGE,{"derivedFrom":subQ5}),1.0]])]});}
            var Q3;
            {var subQ5=sQuery(id+"F10.wireOp",EDGE,"E65");Q3=makeQuery(id+"F10.imprint","IMPRINT",FACE,{"disambiguationData":[TD([[makeQuery(id+"F10.imprint","IMPRINT",EDGE,{"derivedFrom":subQ5}),1.0]])]});}
            var Q4;
            {var subQ5=sQuery(id+"F10.wireOp",EDGE,"E67");Q4=makeQuery(id+"F10.imprint","IMPRINT",FACE,{"disambiguationData":[TD([[makeQuery(id+"F10.imprint","IMPRINT",EDGE,{"derivedFrom":subQ5}),1.0]])]});}
            var Q5;
            {var subQ0=sQuery(id+"F10.wireOp",EDGE,"E33");var subQ5=sQuery(id+"F10.wireOp",EDGE,"E62");var subQ6=makeQuery(id+"F10.imprint","INTERSECT",VERTEX,{"derivedFrom":[subQ0,subQ5]});Q5=makeQuery(id+"F10.imprint","IMPRINT",FACE,{"disambiguationData":[TD([[makeQuery(id+"F10.imprint","IMPRINT",EDGE,{"disambiguationData":[TD([[subQ6,-1.0]])],"derivedFrom":subQ5}),1.0]])]});}
            var Q6;
            {var subQ0=sQuery(id+"F10.wireOp",EDGE,"E61");Q6=makeQuery(id+"F10.imprint","IMPRINT",FACE,{"disambiguationData":[TD([[makeQuery(id+"F10.imprint","IMPRINT",EDGE,{"derivedFrom":subQ0}),1.0]])]});}
            var Q7;
            {var subQ0=sQuery(id+"F10.wireOp",EDGE,"E59");Q7=makeQuery(id+"F10.imprint","IMPRINT",FACE,{"disambiguationData":[TD([[makeQuery(id+"F10.imprint","IMPRINT",EDGE,{"derivedFrom":subQ0}),1.0]])]});}
            extrude(context, id + "F12", {"entities" : qUnion([Q0, Q1, Q2, Q3, Q4, Q5, Q6, Q7]), "operationType" : NewBodyOperationType.REMOVE, "oppositeDirection" : true, "depth" : 25.4 * mm});
        }
        {
            var Q0;
            Q0=makeQuery(id+"F10.imprint","IMPRINT",FACE,{"disambiguationData":[TD([[makeQuery(id+"F10.imprint","IMPRINT",EDGE,{"derivedFrom":sQuery(id+"F10.wireOp",EDGE,"E81")}),1.0]])]});
            var Q1;
            Q1=makeQuery(id+"F10.imprint","IMPRINT",FACE,{"disambiguationData":[TD([[makeQuery(id+"F10.imprint","IMPRINT",EDGE,{"derivedFrom":sQuery(id+"F10.wireOp",EDGE,"E89.MirrorCS")}),-1.0]])]});
            var Q2;
            Q2=makeQuery(id+"F10.imprint","IMPRINT",FACE,{"disambiguationData":[TD([[makeQuery(id+"F10.imprint","IMPRINT",EDGE,{"derivedFrom":sQuery(id+"F10.wireOp",EDGE,"E97.MirrorCS")}),1.0]])]});
            var Q3;
            Q3=makeQuery(id+"F10.imprint","IMPRINT",FACE,{"disambiguationData":[TD([[makeQuery(id+"F10.imprint","IMPRINT",EDGE,{"derivedFrom":sQuery(id+"F10.wireOp",EDGE,"E105.MirrorCS")}),-1.0]])]});
            var Q4;
            Q4=makeQuery(id+"F10.imprint","IMPRINT",FACE,{"disambiguationData":[TD([[makeQuery(id+"F10.imprint","IMPRINT",EDGE,{"derivedFrom":sQuery(id+"F10.wireOp",EDGE,"E113.MirrorCS")}),-1.0]])]});
            var Q5;
            Q5=makeQuery(id+"F10.imprint","IMPRINT",FACE,{"disambiguationData":[TD([[makeQuery(id+"F10.imprint","IMPRINT",EDGE,{"derivedFrom":sQuery(id+"F10.wireOp",EDGE,"E121.MirrorCS")}),1.0]])]});
            extrude(context, id + "F13", {"entities" : qUnion([Q0, Q1, Q2, Q3, Q4, Q5]), "operationType" : NewBodyOperationType.REMOVE, "oppositeDirection" : true, "depth" : 25.4 * mm});
        }
        {
            var Q0;
            {var subQ0=sQuery(id+"F10.wireOp",EDGE,"E78");var subQ1=sQuery(id+"F10.wireOp",EDGE,"E29");var subQ2=makeQuery(id+"F10.imprint","INTERSECT",VERTEX,{"derivedFrom":[subQ1,subQ0]});Q0=makeQuery(id+"F10.imprint","IMPRINT",FACE,{"disambiguationData":[TD([[makeQuery(id+"F10.imprint","IMPRINT",EDGE,{"disambiguationData":[TD([[subQ2,-1.0]])],"derivedFrom":subQ1}),-1.0]])]});}
            var Q1;
            {var subQ0=sQuery(id+"F10.wireOp",EDGE,"E78");var subQ1=sQuery(id+"F10.wireOp",EDGE,"E29");var subQ2=makeQuery(id+"F10.imprint","INTERSECT",VERTEX,{"derivedFrom":[subQ1,subQ0]});Q1=makeQuery(id+"F10.imprint","IMPRINT",FACE,{"disambiguationData":[TD([[makeQuery(id+"F10.imprint","IMPRINT",EDGE,{"disambiguationData":[TD([[subQ2,-1.0]])],"derivedFrom":subQ1}),1.0]])]});}
            extrude(context, id + "F14", {"entities" : qUnion([Q0, Q1]), "operationType" : NewBodyOperationType.REMOVE, "oppositeDirection" : true, "depth" : 25.4 * mm});
        }
        {
            var Q0;
            Q0=makeQuery(id+"F10.imprint","IMPRINT",FACE,{"disambiguationData":[TD([[makeQuery(id+"F10.imprint","IMPRINT",EDGE,{"derivedFrom":sQuery(id+"F10.wireOp",EDGE,"E137.MirrorCS")}),-1.0]])]});
            var Q1;
            Q1=makeQuery(id+"F10.imprint","IMPRINT",FACE,{"disambiguationData":[TD([[makeQuery(id+"F10.imprint","IMPRINT",EDGE,{"derivedFrom":sQuery(id+"F10.wireOp",EDGE,"E145")}),1.0]])]});
            var Q2;
            Q2=makeQuery(id+"F10.imprint","IMPRINT",FACE,{"disambiguationData":[TD([[makeQuery(id+"F10.imprint","IMPRINT",EDGE,{"derivedFrom":sQuery(id+"F10.wireOp",EDGE,"E154.MirrorCS")}),-1.0]])]});
            var Q3;
            Q3=makeQuery(id+"F10.imprint","IMPRINT",FACE,{"disambiguationData":[TD([[makeQuery(id+"F10.imprint","IMPRINT",EDGE,{"derivedFrom":sQuery(id+"F10.wireOp",EDGE,"E129.MirrorCS")}),1.0]])]});
            extrude(context, id + "F15", {"entities" : qUnion([Q0, Q1, Q2, Q3]), "operationType" : NewBodyOperationType.REMOVE, "oppositeDirection" : true, "depth" : 25.4 * mm});
        }
        {
            var Q0;
            {var subQ0=sQuery(id+"F10.wireOp",EDGE,"E162");var subQ1=sQuery(id+"F10.wireOp",EDGE,"E29");var subQ2=makeQuery(id+"F10.imprint","INTERSECT",VERTEX,{"disambiguationData":[OD(0.0)],"derivedFrom":[subQ1,subQ0]});Q0=makeQuery(id+"F10.imprint","IMPRINT",FACE,{"disambiguationData":[TD([[makeQuery(id+"F10.imprint","IMPRINT",EDGE,{"disambiguationData":[TD([[subQ2,-1.0]])],"derivedFrom":subQ1}),-1.0]])]});}
            var Q1;
            {var subQ0=sQuery(id+"F10.wireOp",EDGE,"E162");var subQ1=sQuery(id+"F10.wireOp",EDGE,"E29");var subQ2=makeQuery(id+"F10.imprint","INTERSECT",VERTEX,{"disambiguationData":[OD(0.0)],"derivedFrom":[subQ1,subQ0]});Q1=makeQuery(id+"F10.imprint","IMPRINT",FACE,{"disambiguationData":[TD([[makeQuery(id+"F10.imprint","IMPRINT",EDGE,{"disambiguationData":[TD([[subQ2,-1.0]])],"derivedFrom":subQ1}),1.0]])]});}
            extrude(context, id + "F16", {"entities" : qUnion([Q0, Q1]), "operationType" : NewBodyOperationType.REMOVE, "oppositeDirection" : true, "depth" : 25.4 * mm});
        }
        {
            var Q0;
            Q0=makeQuery(id+"F0.imprint","IMPRINT",FACE,{"disambiguationData":[TD([[makeQuery(id+"F0.imprint","IMPRINT",EDGE,{"derivedFrom":sQuery(id+"F0.wireOp",EDGE,"E13")}),-1.0]])]});
            extrude(context, id + "F17", {"entities" : qUnion([Q0]), "operationType" : NewBodyOperationType.ADD, "depth" : 1.27 * mm});
        }
    });
